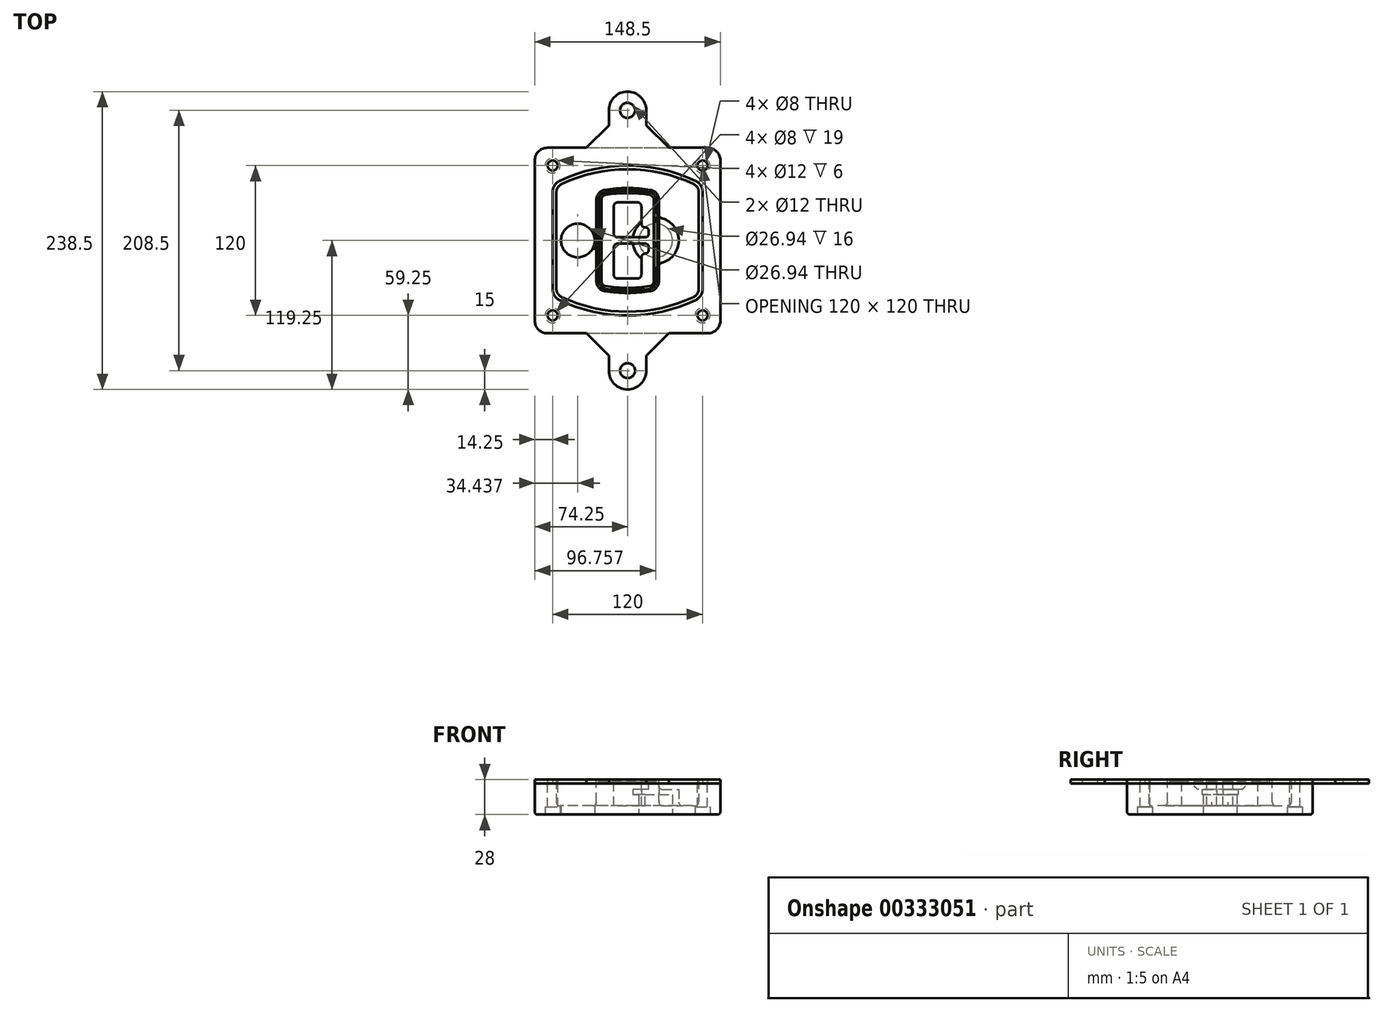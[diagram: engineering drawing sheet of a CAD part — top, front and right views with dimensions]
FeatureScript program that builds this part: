
annotation { "Feature Type Name" : "Feature", "Feature Type Description" : "" }
export const myFeature = defineFeature(function(context is Context, id is Id, definition is map)
    precondition{}
    {
        {
            var Q0;
            Q0=qCreatedBy(makeId("Top.planeOp"),FACE);
            var sketch = newSketch(context, id + "F0", { "sketchPlane" : qUnion([Q0])});
            skPoint(sketch, "E0.rect.middle", {"position": v(0, 0) * mm});
            skLineSegment(sketch, "E1.bottom", {"start": v(-64.25, -74.25) * mm, "end": v(64.25, -74.25) * mm});
            skLineSegment(sketch, "E1.top", {"start": v(-64.25, 74.25) * mm, "end": v(64.25, 74.25) * mm});
            skLineSegment(sketch, "E1.left", {"start": v(-74.25, -64.25) * mm, "end": v(-74.25, 64.25) * mm});
            skLineSegment(sketch, "E1.right", {"start": v(74.25, -64.25) * mm, "end": v(74.25, 64.25) * mm});
            skLineSegment(sketch, "E2", {"start": v(-74.25, 74.25) * mm, "end": v(74.25, -74.25) * mm, "construction": true});
            skLineSegment(sketch, "E3", {"start": v(74.25, 74.25) * mm, "end": v(-74.25, -74.25) * mm, "construction": true});
            skCircle(sketch, "E4", {"center": v(-60, 60) * mm, "radius": 4 * mm});
            skCircle(sketch, "E5", {"center": v(60, 60) * mm, "radius": 4 * mm});
            skCircle(sketch, "E6", {"center": v(60, -60) * mm, "radius": 4 * mm});
            skCircle(sketch, "E7", {"center": v(-60, -60) * mm, "radius": 4 * mm});
            skLineSegment(sketch, "E8", {"start": v(-60, 60) * mm, "end": v(60, 60) * mm, "construction": true});
            skLineSegment(sketch, "E9", {"start": v(60, 60) * mm, "end": v(60, -60) * mm, "construction": true});
            skLineSegment(sketch, "E10", {"start": v(60, -60) * mm, "end": v(-60, -60) * mm, "construction": true});
            skLineSegment(sketch, "E11", {"start": v(-60, -60) * mm, "end": v(-60, 60) * mm, "construction": true});
            skLineSegment(sketch, "E12", {"start": v(-60, 38.83) * mm, "end": v(-60, -38.83) * mm});
            skLineSegment(sketch, "E13", {"start": v(60, 38.83) * mm, "end": v(60, -38.83) * mm});
            skArc(sketch, "E14", {"start": v(54.26, 47.88) * mm, "mid": v(0, 60) * mm, "end": v(-54.26, 47.88) * mm});
            skArc(sketch, "E15", {"start": v(-54.26, -47.88) * mm, "mid": v(0, -60) * mm, "end": v(54.26, -47.88) * mm});
            skLineSegment(sketch, "E16", {"start": v(-60, 0) * mm, "end": v(60, 0) * mm, "construction": true});
            skPoint(sketch, "E17.visualSharp", {"position": v(-60, -45) * mm});
            skArc(sketch, "E17.filletArc", {"start": v(-60, -38.83) * mm, "mid": v(-58.44, -44.2) * mm, "end": v(-54.26, -47.88) * mm});
            skPoint(sketch, "E18.visualSharp", {"position": v(-60, 45) * mm});
            skArc(sketch, "E18.filletArc", {"start": v(-54.26, 47.88) * mm, "mid": v(-58.44, 44.2) * mm, "end": v(-60, 38.83) * mm});
            skPoint(sketch, "E19.visualSharp", {"position": v(60, 45) * mm});
            skArc(sketch, "E19.filletArc", {"start": v(60, 38.83) * mm, "mid": v(58.44, 44.2) * mm, "end": v(54.26, 47.88) * mm});
            skPoint(sketch, "E20.visualSharp", {"position": v(60, -45) * mm});
            skArc(sketch, "E20.filletArc", {"start": v(54.26, -47.88) * mm, "mid": v(58.44, -44.2) * mm, "end": v(60, -38.83) * mm});
            skPoint(sketch, "E21.visualSharp", {"position": v(-74.25, 74.25) * mm});
            skArc(sketch, "E21.filletArc", {"start": v(-64.25, 74.25) * mm, "mid": v(-71.32, 71.32) * mm, "end": v(-74.25, 64.25) * mm});
            skPoint(sketch, "E22.visualSharp", {"position": v(74.25, 74.25) * mm});
            skArc(sketch, "E22.filletArc", {"start": v(74.25, 64.25) * mm, "mid": v(71.32, 71.32) * mm, "end": v(64.25, 74.25) * mm});
            skPoint(sketch, "E23.visualSharp", {"position": v(74.25, -74.25) * mm});
            skArc(sketch, "E23.filletArc", {"start": v(64.25, -74.25) * mm, "mid": v(71.32, -71.32) * mm, "end": v(74.25, -64.25) * mm});
            skPoint(sketch, "E24.visualSharp", {"position": v(-74.25, -74.25) * mm});
            skArc(sketch, "E24.filletArc", {"start": v(-74.25, -64.25) * mm, "mid": v(-71.32, -71.32) * mm, "end": v(-64.25, -74.25) * mm});
            skArc(sketch, "E25.0", {"start": v(57, 38.83) * mm, "mid": v(55.9, 42.58) * mm, "end": v(52.98, 45.17) * mm});
            skLineSegment(sketch, "E25.1", {"start": v(57, 38.83) * mm, "end": v(57, -38.83) * mm});
            skArc(sketch, "E25.2", {"start": v(52.98, -45.17) * mm, "mid": v(55.9, -42.58) * mm, "end": v(57, -38.83) * mm});
            skArc(sketch, "E25.3", {"start": v(-52.98, -45.17) * mm, "mid": v(0, -57) * mm, "end": v(52.98, -45.17) * mm});
            skArc(sketch, "E25.4", {"start": v(-57, -38.83) * mm, "mid": v(-55.9, -42.58) * mm, "end": v(-52.98, -45.17) * mm});
            skArc(sketch, "E25.5", {"start": v(52.98, 45.17) * mm, "mid": v(0, 57) * mm, "end": v(-52.98, 45.17) * mm});
            skLineSegment(sketch, "E25.6", {"start": v(-57, 38.83) * mm, "end": v(-57, -38.83) * mm});
            skArc(sketch, "E25.7", {"start": v(-52.98, 45.17) * mm, "mid": v(-55.9, 42.58) * mm, "end": v(-57, 38.83) * mm});
            skArc(sketch, "E26.0", {"start": v(-55.96, 51.5) * mm, "mid": v(-61.82, 46.33) * mm, "end": v(-64, 38.83) * mm});
            skArc(sketch, "E26.1", {"start": v(55.96, 51.5) * mm, "mid": v(0, 64) * mm, "end": v(-55.96, 51.5) * mm});
            skArc(sketch, "E26.2", {"start": v(64, 38.83) * mm, "mid": v(61.82, 46.33) * mm, "end": v(55.96, 51.5) * mm});
            skLineSegment(sketch, "E26.3", {"start": v(64, 38.83) * mm, "end": v(64, -38.83) * mm});
            skArc(sketch, "E26.4", {"start": v(55.96, -51.5) * mm, "mid": v(61.82, -46.33) * mm, "end": v(64, -38.83) * mm});
            skLineSegment(sketch, "E26.5", {"start": v(-64, 38.83) * mm, "end": v(-64, -38.83) * mm});
            skArc(sketch, "E26.6", {"start": v(-55.96, -51.5) * mm, "mid": v(0, -64) * mm, "end": v(55.96, -51.5) * mm});
            skArc(sketch, "E26.7", {"start": v(-64, -38.83) * mm, "mid": v(-61.82, -46.33) * mm, "end": v(-55.96, -51.5) * mm});
            skSolve(sketch);
        }
        {
            var Q0;
            Q0=makeQuery(id+"F0.imprint","IMPRINT",FACE,{"disambiguationData":[TD([[makeQuery(id+"F0.imprint","IMPRINT",EDGE,{"derivedFrom":sQuery(id+"F0.wireOp",EDGE,"E1.bottom")}),1.0]])]});
            var Q1;
            Q1=makeQuery(id+"F0.imprint","IMPRINT",FACE,{"disambiguationData":[TD([[makeQuery(id+"F0.imprint","IMPRINT",EDGE,{"derivedFrom":sQuery(id+"F0.wireOp",EDGE,"E12")}),1.0]])]});
            var Q2;
            Q2=makeQuery(id+"F0.imprint","IMPRINT",FACE,{"disambiguationData":[TD([[makeQuery(id+"F0.imprint","IMPRINT",EDGE,{"derivedFrom":sQuery(id+"F0.wireOp",EDGE,"E25.0")}),1.0]])]});
            var Q3;
            Q3=makeQuery(id+"F0.imprint","IMPRINT",FACE,{"disambiguationData":[TD([[makeQuery(id+"F0.imprint","IMPRINT",EDGE,{"derivedFrom":sQuery(id+"F0.wireOp",EDGE,"E12")}),-1.0]])]});
            extrude(context, id + "F1", {"entities" : qUnion([Q0, Q1, Q2, Q3]), "oppositeDirection" : true, "depth" : 25 * mm});
        }
        {
            var Q0;
            Q0=makeQuery(id+"F0.imprint","IMPRINT",FACE,{"disambiguationData":[TD([[makeQuery(id+"F0.imprint","IMPRINT",EDGE,{"derivedFrom":sQuery(id+"F0.wireOp",EDGE,"E12")}),1.0]])]});
            extrude(context, id + "F2", {"entities" : qUnion([Q0]), "operationType" : NewBodyOperationType.ADD, "depth" : 3 * mm});
        }
        {
            var Q0;
            Q0=makeQuery(id+"F0.imprint","IMPRINT",FACE,{"disambiguationData":[TD([[makeQuery(id+"F0.imprint","IMPRINT",EDGE,{"derivedFrom":sQuery(id+"F0.wireOp",EDGE,"E25.0")}),1.0]])]});
            extrude(context, id + "F3", {"entities" : qUnion([Q0]), "operationType" : NewBodyOperationType.REMOVE, "oppositeDirection" : true, "depth" : 18 * mm});
        }
        {
            var Q0;
            Q0=makeQuery(id+"F2.opExtrude","CAP_FACE",FACE,{"disambiguationData":[OSD([sQuery(id+"F0.wireOp",EDGE,"E12"),sQuery(id+"F0.wireOp",EDGE,"E13"),sQuery(id+"F0.wireOp",EDGE,"E14"),sQuery(id+"F0.wireOp",EDGE,"E15"),sQuery(id+"F0.wireOp",EDGE,"E17.filletArc"),sQuery(id+"F0.wireOp",EDGE,"E18.filletArc"),sQuery(id+"F0.wireOp",EDGE,"E19.filletArc"),sQuery(id+"F0.wireOp",EDGE,"E20.filletArc"),sQuery(id+"F0.wireOp",EDGE,"E25.0"),sQuery(id+"F0.wireOp",EDGE,"E25.1"),sQuery(id+"F0.wireOp",EDGE,"E25.2"),sQuery(id+"F0.wireOp",EDGE,"E25.3"),sQuery(id+"F0.wireOp",EDGE,"E25.4"),sQuery(id+"F0.wireOp",EDGE,"E25.5"),sQuery(id+"F0.wireOp",EDGE,"E25.6"),sQuery(id+"F0.wireOp",EDGE,"E25.7")])],"isStart":false});
            var sketch = newSketch(context, id + "F4", { "sketchPlane" : qUnion([Q0])});
            skArc(sketch, "E27.0", {"start": v(-18.34, -40.45) * mm, "mid": v(0, -42) * mm, "end": v(18.34, -40.45) * mm});
            skArc(sketch, "E28.0", {"start": v(18.34, 40.45) * mm, "mid": v(0, 42) * mm, "end": v(-18.34, 40.45) * mm});
            skLineSegment(sketch, "E29", {"start": v(-25, 32.57) * mm, "end": v(-25, -32.57) * mm});
            skLineSegment(sketch, "E30", {"start": v(25, 32.57) * mm, "end": v(25, -32.57) * mm});
            skLineSegment(sketch, "E31", {"start": v(-25, 39.1) * mm, "end": v(25, 39.1) * mm, "construction": true});
            skLineSegment(sketch, "E32", {"start": v(-25, -39.1) * mm, "end": v(25, -39.1) * mm, "construction": true});
            skPoint(sketch, "E33.visualSharp", {"position": v(-25, 39.1) * mm});
            skArc(sketch, "E33.filletArc", {"start": v(-18.34, 40.45) * mm, "mid": v(-23.11, 37.73) * mm, "end": v(-25, 32.57) * mm});
            skPoint(sketch, "E34.visualSharp", {"position": v(25, 39.1) * mm});
            skArc(sketch, "E34.filletArc", {"start": v(25, 32.57) * mm, "mid": v(23.11, 37.73) * mm, "end": v(18.34, 40.45) * mm});
            skPoint(sketch, "E35.visualSharp", {"position": v(25, -39.1) * mm});
            skArc(sketch, "E35.filletArc", {"start": v(18.34, -40.45) * mm, "mid": v(23.11, -37.73) * mm, "end": v(25, -32.57) * mm});
            skPoint(sketch, "E36.visualSharp", {"position": v(-25, -39.1) * mm});
            skArc(sketch, "E36.filletArc", {"start": v(-25, -32.57) * mm, "mid": v(-23.11, -37.73) * mm, "end": v(-18.34, -40.45) * mm});
            skArc(sketch, "E37.0", {"start": v(52.98, 45.17) * mm, "mid": v(0, 57) * mm, "end": v(-52.98, 45.17) * mm});
            skArc(sketch, "E37.1", {"start": v(-52.98, 45.17) * mm, "mid": v(-55.9, 42.58) * mm, "end": v(-57, 38.83) * mm});
            skLineSegment(sketch, "E37.2", {"start": v(-57, 38.83) * mm, "end": v(-57, -38.83) * mm});
            skArc(sketch, "E37.3", {"start": v(-57, -38.83) * mm, "mid": v(-55.9, -42.58) * mm, "end": v(-52.98, -45.17) * mm});
            skArc(sketch, "E37.4", {"start": v(-52.98, -45.17) * mm, "mid": v(0, -57) * mm, "end": v(52.98, -45.17) * mm});
            skArc(sketch, "E37.5", {"start": v(52.98, -45.17) * mm, "mid": v(55.9, -42.58) * mm, "end": v(57, -38.83) * mm});
            skLineSegment(sketch, "E37.6", {"start": v(57, 38.83) * mm, "end": v(57, -38.83) * mm});
            skArc(sketch, "E37.7", {"start": v(57, 38.83) * mm, "mid": v(55.9, 42.58) * mm, "end": v(52.98, 45.17) * mm});
            skLineSegment(sketch, "E38.0", {"start": v(23, 32.57) * mm, "end": v(23, -32.57) * mm});
            skArc(sketch, "E38.1", {"start": v(18, -38.48) * mm, "mid": v(21.58, -36.44) * mm, "end": v(23, -32.57) * mm});
            skArc(sketch, "E38.2", {"start": v(-18, -38.48) * mm, "mid": v(0, -40) * mm, "end": v(18, -38.48) * mm});
            skArc(sketch, "E38.3", {"start": v(-23, -32.57) * mm, "mid": v(-21.58, -36.44) * mm, "end": v(-18, -38.48) * mm});
            skLineSegment(sketch, "E38.4", {"start": v(-23, 32.57) * mm, "end": v(-23, -32.57) * mm});
            skArc(sketch, "E38.5", {"start": v(23, 32.57) * mm, "mid": v(21.58, 36.44) * mm, "end": v(18, 38.48) * mm});
            skArc(sketch, "E38.6", {"start": v(-18, 38.48) * mm, "mid": v(-21.58, 36.44) * mm, "end": v(-23, 32.57) * mm});
            skArc(sketch, "E38.7", {"start": v(18, 38.48) * mm, "mid": v(0, 40) * mm, "end": v(-18, 38.48) * mm});
            skArc(sketch, "E39.0", {"start": v(21, 32.57) * mm, "mid": v(20.06, 35.15) * mm, "end": v(17.67, 36.5) * mm});
            skLineSegment(sketch, "E39.1", {"start": v(21, 32.57) * mm, "end": v(21, -32.57) * mm});
            skArc(sketch, "E39.2", {"start": v(17.67, -36.5) * mm, "mid": v(20.06, -35.15) * mm, "end": v(21, -32.57) * mm});
            skArc(sketch, "E39.3", {"start": v(-17.67, -36.5) * mm, "mid": v(0, -38) * mm, "end": v(17.67, -36.5) * mm});
            skArc(sketch, "E39.4", {"start": v(-21, -32.57) * mm, "mid": v(-20.06, -35.15) * mm, "end": v(-17.67, -36.5) * mm});
            skArc(sketch, "E39.5", {"start": v(17.67, 36.5) * mm, "mid": v(0, 38) * mm, "end": v(-17.67, 36.5) * mm});
            skLineSegment(sketch, "E39.6", {"start": v(-21, 32.57) * mm, "end": v(-21, -32.57) * mm});
            skArc(sketch, "E39.7", {"start": v(-17.67, 36.5) * mm, "mid": v(-20.06, 35.15) * mm, "end": v(-21, 32.57) * mm});
            skLineSegment(sketch, "E40", {"start": v(-25, 0) * mm, "end": v(25, 0) * mm, "construction": true});
            skLineSegment(sketch, "E41", {"start": v(-11, 5.5) * mm, "end": v(-11, 27.5) * mm});
            skLineSegment(sketch, "E42", {"start": v(-8, 30.5) * mm, "end": v(8, 30.5) * mm});
            skLineSegment(sketch, "E43", {"start": v(11, 27.5) * mm, "end": v(11, 13.5) * mm});
            skLineSegment(sketch, "E44", {"start": v(14, 10.5) * mm, "end": v(14, 10.5) * mm});
            skLineSegment(sketch, "E45", {"start": v(17, 7.5) * mm, "end": v(17, 5.5) * mm});
            skLineSegment(sketch, "E46", {"start": v(14, 2.5) * mm, "end": v(-8, 2.5) * mm});
            skPoint(sketch, "E47.visualSharp", {"position": v(-11, 30.5) * mm});
            skArc(sketch, "E47.filletArc", {"start": v(-8, 30.5) * mm, "mid": v(-10.12, 29.62) * mm, "end": v(-11, 27.5) * mm});
            skPoint(sketch, "E48.visualSharp", {"position": v(11, 30.5) * mm});
            skArc(sketch, "E48.filletArc", {"start": v(11, 27.5) * mm, "mid": v(10.12, 29.62) * mm, "end": v(8, 30.5) * mm});
            skPoint(sketch, "E49.visualSharp", {"position": v(11, 10.5) * mm});
            skArc(sketch, "E49.filletArc", {"start": v(11, 13.5) * mm, "mid": v(11.88, 11.38) * mm, "end": v(14, 10.5) * mm});
            skPoint(sketch, "E50.visualSharp", {"position": v(17, 10.5) * mm});
            skArc(sketch, "E50.filletArc", {"start": v(17, 7.5) * mm, "mid": v(16.12, 9.62) * mm, "end": v(14, 10.5) * mm});
            skPoint(sketch, "E51.visualSharp", {"position": v(17, 2.5) * mm});
            skArc(sketch, "E51.filletArc", {"start": v(14, 2.5) * mm, "mid": v(16.12, 3.38) * mm, "end": v(17, 5.5) * mm});
            skPoint(sketch, "E52.visualSharp", {"position": v(-11, 2.5) * mm});
            skArc(sketch, "E52.filletArc", {"start": v(-11, 5.5) * mm, "mid": v(-10.12, 3.38) * mm, "end": v(-8, 2.5) * mm});
            skLineSegment(sketch, "E53.0.MirrorCS", {"start": v(14, -2.5) * mm, "end": v(-8, -2.5) * mm});
            skArc(sketch, "E54.0.MirrorCS", {"start": v(-11, -5.5) * mm, "mid": v(-10.12, -3.38) * mm, "end": v(-8, -2.5) * mm});
            skLineSegment(sketch, "E55.0.MirrorCS", {"start": v(-11, -5.5) * mm, "end": v(-11, -27.5) * mm});
            skArc(sketch, "E56.0.MirrorCS", {"start": v(-8, -30.5) * mm, "mid": v(-10.12, -29.62) * mm, "end": v(-11, -27.5) * mm});
            skLineSegment(sketch, "E57.0.MirrorCS", {"start": v(-8, -30.5) * mm, "end": v(8, -30.5) * mm});
            skArc(sketch, "E58.0.MirrorCS", {"start": v(11, -27.5) * mm, "mid": v(10.12, -29.62) * mm, "end": v(8, -30.5) * mm});
            skLineSegment(sketch, "E59.0.MirrorCS", {"start": v(11, -27.5) * mm, "end": v(11, -13.5) * mm});
            skArc(sketch, "E60.0.MirrorCS", {"start": v(11, -13.5) * mm, "mid": v(11.88, -11.38) * mm, "end": v(14, -10.5) * mm});
            skArc(sketch, "E61.0.MirrorCS", {"start": v(17, -7.5) * mm, "mid": v(16.12, -9.62) * mm, "end": v(14, -10.5) * mm});
            skLineSegment(sketch, "E62.0.MirrorCS", {"start": v(17, -7.5) * mm, "end": v(17, -5.5) * mm});
            skArc(sketch, "E63.0.MirrorCS", {"start": v(14, -2.5) * mm, "mid": v(16.12, -3.38) * mm, "end": v(17, -5.5) * mm});
            skSolve(sketch);
        }
        {
            var Q0;
            Q0=makeQuery(id+"F4.imprint","IMPRINT",FACE,{"disambiguationData":[TD([[makeQuery(id+"F4.imprint","IMPRINT",EDGE,{"derivedFrom":sQuery(id+"F4.wireOp",EDGE,"E27.0")}),1.0]])]});
            var Q1;
            Q1=makeQuery(id+"F4.imprint","IMPRINT",FACE,{"disambiguationData":[TD([[makeQuery(id+"F4.imprint","IMPRINT",EDGE,{"derivedFrom":sQuery(id+"F4.wireOp",EDGE,"E38.0")}),-1.0]])]});
            var Q2;
            Q2=makeQuery(id+"F4.imprint","IMPRINT",FACE,{"disambiguationData":[TD([[makeQuery(id+"F4.imprint","IMPRINT",EDGE,{"derivedFrom":sQuery(id+"F4.wireOp",EDGE,"E39.0")}),1.0]])]});
            extrude(context, id + "F5", {"entities" : qUnion([Q0, Q1, Q2]), "operationType" : NewBodyOperationType.ADD, "endBound" : BoundingType.UP_TO_NEXT, "oppositeDirection" : true, "depth" : 25 * mm});
        }
        {
            var Q0;
            Q0=makeQuery(id+"F4.imprint","IMPRINT",FACE,{"disambiguationData":[TD([[makeQuery(id+"F4.imprint","IMPRINT",EDGE,{"derivedFrom":sQuery(id+"F4.wireOp",EDGE,"E38.0")}),-1.0]])]});
            extrude(context, id + "F6", {"entities" : qUnion([Q0]), "operationType" : NewBodyOperationType.REMOVE, "oppositeDirection" : true, "depth" : 2 * mm});
        }
        {
            var Q0;
            Q0=makeQuery(id+"F1.opExtrude","CAP_FACE",FACE,{"disambiguationData":[OSD([sQuery(id+"F0.wireOp",EDGE,"E1.bottom"),sQuery(id+"F0.wireOp",EDGE,"E1.top"),sQuery(id+"F0.wireOp",EDGE,"E1.left"),sQuery(id+"F0.wireOp",EDGE,"E1.right"),sQuery(id+"F0.wireOp",EDGE,"E4"),sQuery(id+"F0.wireOp",EDGE,"E5"),sQuery(id+"F0.wireOp",EDGE,"E6"),sQuery(id+"F0.wireOp",EDGE,"E7"),sQuery(id+"F0.wireOp",EDGE,"E21.filletArc"),sQuery(id+"F0.wireOp",EDGE,"E22.filletArc"),sQuery(id+"F0.wireOp",EDGE,"E23.filletArc"),sQuery(id+"F0.wireOp",EDGE,"E24.filletArc")])],"isStart":false});
            var sketch = newSketch(context, id + "F7", { "sketchPlane" : qUnion([Q0])});
            skCircle(sketch, "E64", {"center": v(22.5, 0) * mm, "radius": 13.47 * mm});
            skCircle(sketch, "E65", {"center": v(-39.81, 0) * mm, "radius": 13.47 * mm});
            skLineSegment(sketch, "E66", {"start": v(74.25, 0) * mm, "end": v(-74.25, 0) * mm});
            skCircle(sketch, "E67", {"center": v(22.5, 0) * mm, "radius": 18.47 * mm});
            skCircle(sketch, "E68", {"center": v(60, -60) * mm, "radius": 6 * mm});
            skCircle(sketch, "E69", {"center": v(-60, -60) * mm, "radius": 6 * mm});
            skCircle(sketch, "E70", {"center": v(-60, 60) * mm, "radius": 6 * mm});
            skCircle(sketch, "E71", {"center": v(60, 60) * mm, "radius": 6 * mm});
            skSolve(sketch);
        }
        {
            var Q0;
            {var subQ1=sQuery(id+"F7.wireOp",EDGE,"E66");var subQ4=sQuery(id+"F7.wireOp",EDGE,"E64");var subQ6=makeQuery(id+"F7.imprint","INTERSECT",VERTEX,{"disambiguationData":[OD(0.0)],"derivedFrom":[subQ4,subQ1]});Q0=makeQuery(id+"F7.imprint","IMPRINT",FACE,{"disambiguationData":[TD([[makeQuery(id+"F7.imprint","IMPRINT",EDGE,{"disambiguationData":[TD([[subQ6,-1.0]])],"derivedFrom":subQ4}),-1.0]])]});}
            var Q1;
            {var subQ0=sQuery(id+"F7.wireOp",EDGE,"E66");var subQ1=sQuery(id+"F7.wireOp",EDGE,"E64");var subQ3=makeQuery(id+"F7.imprint","INTERSECT",VERTEX,{"disambiguationData":[OD(0.0)],"derivedFrom":[subQ1,subQ0]});Q1=makeQuery(id+"F7.imprint","IMPRINT",FACE,{"disambiguationData":[TD([[makeQuery(id+"F7.imprint","IMPRINT",EDGE,{"disambiguationData":[TD([[subQ3,-1.0]])],"derivedFrom":subQ1}),1.0]])]});}
            var Q2;
            {var subQ0=sQuery(id+"F7.wireOp",EDGE,"E66");var subQ1=sQuery(id+"F7.wireOp",EDGE,"E64");var subQ3=makeQuery(id+"F7.imprint","INTERSECT",VERTEX,{"disambiguationData":[OD(0.0)],"derivedFrom":[subQ1,subQ0]});Q2=makeQuery(id+"F7.imprint","IMPRINT",FACE,{"disambiguationData":[TD([[makeQuery(id+"F7.imprint","IMPRINT",EDGE,{"disambiguationData":[TD([[subQ3,1.0]])],"derivedFrom":subQ1}),1.0]])]});}
            var Q3;
            {var subQ1=sQuery(id+"F7.wireOp",EDGE,"E66");var subQ4=sQuery(id+"F7.wireOp",EDGE,"E64");var subQ6=makeQuery(id+"F7.imprint","INTERSECT",VERTEX,{"disambiguationData":[OD(0.0)],"derivedFrom":[subQ4,subQ1]});Q3=makeQuery(id+"F7.imprint","IMPRINT",FACE,{"disambiguationData":[TD([[makeQuery(id+"F7.imprint","IMPRINT",EDGE,{"disambiguationData":[TD([[subQ6,1.0]])],"derivedFrom":subQ4}),-1.0]])]});}
            extrude(context, id + "F8", {"entities" : qUnion([Q0, Q1, Q2, Q3]), "operationType" : NewBodyOperationType.ADD, "oppositeDirection" : true, "depth" : 20 * mm});
        }
        {
            var Q0;
            {var subQ0=sQuery(id+"F7.wireOp",EDGE,"E66");var subQ1=sQuery(id+"F7.wireOp",EDGE,"E64");var subQ3=makeQuery(id+"F7.imprint","INTERSECT",VERTEX,{"disambiguationData":[OD(0.0)],"derivedFrom":[subQ1,subQ0]});Q0=makeQuery(id+"F7.imprint","IMPRINT",FACE,{"disambiguationData":[TD([[makeQuery(id+"F7.imprint","IMPRINT",EDGE,{"disambiguationData":[TD([[subQ3,-1.0]])],"derivedFrom":subQ1}),1.0]])]});}
            var Q1;
            {var subQ0=sQuery(id+"F7.wireOp",EDGE,"E66");var subQ1=sQuery(id+"F7.wireOp",EDGE,"E64");var subQ3=makeQuery(id+"F7.imprint","INTERSECT",VERTEX,{"disambiguationData":[OD(0.0)],"derivedFrom":[subQ1,subQ0]});Q1=makeQuery(id+"F7.imprint","IMPRINT",FACE,{"disambiguationData":[TD([[makeQuery(id+"F7.imprint","IMPRINT",EDGE,{"disambiguationData":[TD([[subQ3,1.0]])],"derivedFrom":subQ1}),1.0]])]});}
            extrude(context, id + "F9", {"entities" : qUnion([Q0, Q1]), "operationType" : NewBodyOperationType.REMOVE, "oppositeDirection" : true, "depth" : 16 * mm});
        }
        {
            var Q0;
            {var subQ0=sQuery(id+"F7.wireOp",EDGE,"E66");var subQ1=sQuery(id+"F7.wireOp",EDGE,"E65");var subQ3=makeQuery(id+"F7.imprint","INTERSECT",VERTEX,{"disambiguationData":[OD(0.0)],"derivedFrom":[subQ1,subQ0]});Q0=makeQuery(id+"F7.imprint","IMPRINT",FACE,{"disambiguationData":[TD([[makeQuery(id+"F7.imprint","IMPRINT",EDGE,{"disambiguationData":[TD([[subQ3,-1.0]])],"derivedFrom":subQ1}),1.0]])]});}
            var Q1;
            {var subQ0=sQuery(id+"F7.wireOp",EDGE,"E66");var subQ1=sQuery(id+"F7.wireOp",EDGE,"E65");var subQ3=makeQuery(id+"F7.imprint","INTERSECT",VERTEX,{"disambiguationData":[OD(0.0)],"derivedFrom":[subQ1,subQ0]});Q1=makeQuery(id+"F7.imprint","IMPRINT",FACE,{"disambiguationData":[TD([[makeQuery(id+"F7.imprint","IMPRINT",EDGE,{"disambiguationData":[TD([[subQ3,1.0]])],"derivedFrom":subQ1}),1.0]])]});}
            extrude(context, id + "F10", {"entities" : qUnion([Q0, Q1]), "operationType" : NewBodyOperationType.REMOVE, "oppositeDirection" : true, "depth" : 25 * mm});
        }
        {
            var Q0;
            Q0=makeQuery(id+"F7.imprint","IMPRINT",FACE,{"disambiguationData":[TD([[makeQuery(id+"F7.imprint","IMPRINT",EDGE,{"derivedFrom":sQuery(id+"F7.wireOp",EDGE,"E68")}),1.0]])]});
            var Q1;
            Q1=makeQuery(id+"F7.imprint","IMPRINT",FACE,{"disambiguationData":[TD([[makeQuery(id+"F7.imprint","IMPRINT",EDGE,{"derivedFrom":makeQuery(id+"F1.opExtrude","CAP_EDGE",EDGE,{"disambiguationData":[OSD([sQuery(id+"F0.wireOp",EDGE,"E5")])],"isStart":false})}),-1.0]])]});
            var Q2;
            Q2=makeQuery(id+"F7.imprint","IMPRINT",FACE,{"disambiguationData":[TD([[makeQuery(id+"F7.imprint","IMPRINT",EDGE,{"derivedFrom":sQuery(id+"F7.wireOp",EDGE,"E69")}),1.0]])]});
            var Q3;
            Q3=makeQuery(id+"F7.imprint","IMPRINT",FACE,{"disambiguationData":[TD([[makeQuery(id+"F7.imprint","IMPRINT",EDGE,{"derivedFrom":makeQuery(id+"F1.opExtrude","CAP_EDGE",EDGE,{"disambiguationData":[OSD([sQuery(id+"F0.wireOp",EDGE,"E4")])],"isStart":false})}),-1.0]])]});
            var Q4;
            Q4=makeQuery(id+"F7.imprint","IMPRINT",FACE,{"disambiguationData":[TD([[makeQuery(id+"F7.imprint","IMPRINT",EDGE,{"derivedFrom":sQuery(id+"F7.wireOp",EDGE,"E70")}),1.0]])]});
            var Q5;
            Q5=makeQuery(id+"F7.imprint","IMPRINT",FACE,{"disambiguationData":[TD([[makeQuery(id+"F7.imprint","IMPRINT",EDGE,{"derivedFrom":makeQuery(id+"F1.opExtrude","CAP_EDGE",EDGE,{"disambiguationData":[OSD([sQuery(id+"F0.wireOp",EDGE,"E7")])],"isStart":false})}),-1.0]])]});
            var Q6;
            Q6=makeQuery(id+"F7.imprint","IMPRINT",FACE,{"disambiguationData":[TD([[makeQuery(id+"F7.imprint","IMPRINT",EDGE,{"derivedFrom":sQuery(id+"F7.wireOp",EDGE,"E71")}),1.0]])]});
            var Q7;
            Q7=makeQuery(id+"F7.imprint","IMPRINT",FACE,{"disambiguationData":[TD([[makeQuery(id+"F7.imprint","IMPRINT",EDGE,{"derivedFrom":makeQuery(id+"F1.opExtrude","CAP_EDGE",EDGE,{"disambiguationData":[OSD([sQuery(id+"F0.wireOp",EDGE,"E6")])],"isStart":false})}),-1.0]])]});
            extrude(context, id + "F11", {"entities" : qUnion([Q0, Q1, Q2, Q3, Q4, Q5, Q6, Q7]), "operationType" : NewBodyOperationType.REMOVE, "oppositeDirection" : true, "depth" : 6 * mm});
        }
        {
            var Q0;
            Q0=makeQuery(id+"F9.boolean.opBoolean","COPY",FACE,{"derivedFrom":makeQuery(id+"F9.opExtrude","CAP_FACE",FACE,{"disambiguationData":[OSD([sQuery(id+"F7.wireOp",EDGE,"E64")])],"isStart":false})});
            var sketch = newSketch(context, id + "F12", { "sketchPlane" : qUnion([Q0])});
            skArc(sketch, "E72.0", {"start": v(11, 14.45) * mm, "mid": v(6.45, 9.13) * mm, "end": v(4.2, 2.5) * mm});
            skArc(sketch, "E72.1", {"start": v(4.2, -2.5) * mm, "mid": v(6.45, -9.13) * mm, "end": v(11, -14.45) * mm});
            skLineSegment(sketch, "E73", {"start": v(4.2, -2.5) * mm, "end": v(14, -2.5) * mm});
            skLineSegment(sketch, "E74.0", {"start": v(14, 2.5) * mm, "end": v(4.2, 2.5) * mm});
            skArc(sketch, "E74.1", {"start": v(14, 2.5) * mm, "mid": v(16.12, 3.38) * mm, "end": v(17, 5.5) * mm});
            skLineSegment(sketch, "E74.2", {"start": v(17, 7.5) * mm, "end": v(17, 5.5) * mm});
            skArc(sketch, "E74.3", {"start": v(17, 7.5) * mm, "mid": v(16.12, 9.62) * mm, "end": v(14, 10.5) * mm});
            skArc(sketch, "E74.4", {"start": v(11, 13.5) * mm, "mid": v(11.88, 11.38) * mm, "end": v(14, 10.5) * mm});
            skLineSegment(sketch, "E74.5", {"start": v(11, 14.45) * mm, "end": v(11, 13.5) * mm});
            skLineSegment(sketch, "E74.7", {"start": v(14, -2.5) * mm, "end": v(4.2, -2.5) * mm});
            skArc(sketch, "E74.8", {"start": v(14, -2.5) * mm, "mid": v(16.12, -3.38) * mm, "end": v(17, -5.5) * mm});
            skLineSegment(sketch, "E74.9", {"start": v(17, -7.5) * mm, "end": v(17, -5.5) * mm});
            skArc(sketch, "E74.10", {"start": v(17, -7.5) * mm, "mid": v(16.12, -9.62) * mm, "end": v(14, -10.5) * mm});
            skArc(sketch, "E74.11", {"start": v(11, -13.5) * mm, "mid": v(11.88, -11.38) * mm, "end": v(14, -10.5) * mm});
            skLineSegment(sketch, "E74.12", {"start": v(11, -14.45) * mm, "end": v(11, -13.5) * mm});
            skPoint(sketch, "E75.orphan", {"position": v(11, -27.5) * mm});
            skPoint(sketch, "E76.orphan", {"position": v(-8, -2.5) * mm});
            skPoint(sketch, "E77.orphan", {"position": v(-8, 2.5) * mm});
            skPoint(sketch, "E78.orphan", {"position": v(11, 27.5) * mm});
            skSolve(sketch);
        }
        {
            var Q0;
            {var subQ7=sQuery(id+"F12.wireOp",EDGE,"E72.0");var subQ14=sQuery(id+"F12.wireOp",EDGE,"E72.1");var subQ16=sQuery(id+"F12.wireOp",EDGE,"E74.1");var subQ18=sQuery(id+"F12.wireOp",EDGE,"E74.8");Q0=qUnion([makeQuery(id+"F12.imprint","IMPRINT",FACE,{"disambiguationData":[TD([[makeQuery(id+"F12.imprint","IMPRINT",EDGE,{"derivedFrom":subQ7}),1.0]])]}),makeQuery(id+"F12.imprint","IMPRINT",FACE,{"disambiguationData":[TD([[makeQuery(id+"F12.imprint","IMPRINT",EDGE,{"derivedFrom":subQ14}),1.0]])]}),makeQuery(id+"F12.imprint","IMPRINT",FACE,{"disambiguationData":[TD([[makeQuery(id+"F12.imprint","IMPRINT",EDGE,{"derivedFrom":subQ16}),1.0]])]}),makeQuery(id+"F12.imprint","IMPRINT",FACE,{"disambiguationData":[TD([[makeQuery(id+"F12.imprint","IMPRINT",EDGE,{"derivedFrom":subQ18}),-1.0]])]})]);}
            var Q1;
            Q1=makeQuery(id+"F5.boolean.opBoolean","SPLIT",FACE,{"disambiguationData":[TD([makeQuery(id+"F5.opExtrude","SWEPT_FACE",FACE,{"disambiguationData":[OSD([sQuery(id+"F4.wireOp",EDGE,"E41")])]})])],"derivedFrom":makeQuery(id+"F3.boolean.opBoolean","COPY",FACE,{"derivedFrom":makeQuery(id+"F3.opExtrude","CAP_FACE",FACE,{"disambiguationData":[OSD([sQuery(id+"F0.wireOp",EDGE,"E25.0"),sQuery(id+"F0.wireOp",EDGE,"E25.1"),sQuery(id+"F0.wireOp",EDGE,"E25.2"),sQuery(id+"F0.wireOp",EDGE,"E25.3"),sQuery(id+"F0.wireOp",EDGE,"E25.4"),sQuery(id+"F0.wireOp",EDGE,"E25.5"),sQuery(id+"F0.wireOp",EDGE,"E25.6"),sQuery(id+"F0.wireOp",EDGE,"E25.7")])],"isStart":false})})});
            extrude(context, id + "F13", {"entities" : qUnion([Q0]), "operationType" : NewBodyOperationType.REMOVE, "endBound" : BoundingType.UP_TO_SURFACE, "endBoundEntityFace" : qUnion([Q1]), "depth" : 25 * mm});
        }
        {
            var Q0;
            Q0=makeQuery(id+"F3.boolean.opBoolean","COPY",EDGE,{"derivedFrom":makeQuery(id+"F3.opExtrude","CAP_EDGE",EDGE,{"disambiguationData":[OSD([sQuery(id+"F0.wireOp",EDGE,"E25.6")])],"isStart":false})});
            var Q1;
            Q1=makeQuery(id+"F8.boolean.opBoolean","INTERSECT",EDGE,{"derivedFrom":[makeQuery(id+"F5.opExtrude","SWEPT_FACE",FACE,{"disambiguationData":[OSD([sQuery(id+"F4.wireOp",EDGE,"E30")])]}),makeQuery(id+"F8.opExtrude","CAP_FACE",FACE,{"disambiguationData":[OSD([sQuery(id+"F7.wireOp",EDGE,"E67")])],"isStart":false})]});
            var Q2;
            Q2=makeQuery(id+"F8.boolean.opBoolean","INTERSECT",EDGE,{"disambiguationData":[OD(1.0)],"derivedFrom":[makeQuery(id+"F5.opExtrude","SWEPT_FACE",FACE,{"disambiguationData":[OSD([sQuery(id+"F4.wireOp",EDGE,"E30")])]}),makeQuery(id+"F8.opExtrude","SWEPT_FACE",FACE,{"disambiguationData":[OSD([sQuery(id+"F7.wireOp",EDGE,"E67")])]})]});
            var Q3;
            {var subQ0=sQuery(id+"F4.wireOp",EDGE,"E30");Q3=makeQuery(id+"F8.boolean.opBoolean","SPLIT",EDGE,{"disambiguationData":[TD([makeQuery(id+"F5.opExtrude","SWEPT_FACE",FACE,{"disambiguationData":[OSD([sQuery(id+"F4.wireOp",EDGE,"E35.filletArc")])]})])],"derivedFrom":makeQuery(id+"F5.opExtrude","CAP_EDGE",EDGE,{"disambiguationData":[OSD([subQ0])],"isStart":false})});}
            var Q4;
            {var subQ0=sQuery(id+"F0.wireOp",EDGE,"E25.7");var subQ1=sQuery(id+"F0.wireOp",EDGE,"E25.1");var subQ2=sQuery(id+"F0.wireOp",EDGE,"E25.6");var subQ3=sQuery(id+"F0.wireOp",EDGE,"E25.5");var subQ4=sQuery(id+"F0.wireOp",EDGE,"E25.4");var subQ5=sQuery(id+"F0.wireOp",EDGE,"E25.0");var subQ6=sQuery(id+"F0.wireOp",EDGE,"E25.2");var subQ7=sQuery(id+"F0.wireOp",EDGE,"E25.3");Q4=makeQuery(id+"F8.boolean.opBoolean","INTERSECT",EDGE,{"derivedFrom":[makeQuery(id+"F5.boolean.opBoolean","SPLIT",FACE,{"disambiguationData":[TD([makeQuery(id+"F2.opExtrude","SWEPT_FACE",FACE,{"disambiguationData":[OSD([subQ5])]})])],"derivedFrom":makeQuery(id+"F3.boolean.opBoolean","COPY",FACE,{"derivedFrom":makeQuery(id+"F3.opExtrude","CAP_FACE",FACE,{"disambiguationData":[OSD([subQ5,subQ1,subQ6,subQ7,subQ4,subQ3,subQ2,subQ0])],"isStart":false})})}),makeQuery(id+"F8.opExtrude","SWEPT_FACE",FACE,{"disambiguationData":[OSD([sQuery(id+"F7.wireOp",EDGE,"E67")])]})]});}
            var Q5;
            Q5=makeQuery(id+"F8.boolean.opBoolean","INTERSECT",EDGE,{"disambiguationData":[OD(0.0)],"derivedFrom":[makeQuery(id+"F5.opExtrude","SWEPT_FACE",FACE,{"disambiguationData":[OSD([sQuery(id+"F4.wireOp",EDGE,"E30")])]}),makeQuery(id+"F8.opExtrude","SWEPT_FACE",FACE,{"disambiguationData":[OSD([sQuery(id+"F7.wireOp",EDGE,"E67")])]})]});
            fillet(context, id + "F14", {"entities" : qUnion([Q0, Q1, Q2, Q3, Q4, Q5]), "radius" : 3 * mm, "tangentPropagation" : true, "allowEdgeOverflow" : false});
        }
        {
            var Q0;
            Q0=makeQuery(id+"F1.opExtrude","CAP_EDGE",EDGE,{"disambiguationData":[OSD([sQuery(id+"F0.wireOp",EDGE,"E1.bottom")])],"isStart":false});
            fillet(context, id + "F15", {"entities" : qUnion([Q0]), "radius" : 2 * mm, "tangentPropagation" : true, "allowEdgeOverflow" : false});
        }
        {
            var Q0;
            {var subQ0=sQuery(id+"F0.wireOp",EDGE,"E21.filletArc");var subQ1=sQuery(id+"F0.wireOp",EDGE,"E7");var subQ2=sQuery(id+"F0.wireOp",EDGE,"E6");var subQ3=sQuery(id+"F0.wireOp",EDGE,"E5");var subQ4=sQuery(id+"F0.wireOp",EDGE,"E4");var subQ5=sQuery(id+"F0.wireOp",EDGE,"E22.filletArc");var subQ6=sQuery(id+"F0.wireOp",EDGE,"E1.bottom");var subQ7=sQuery(id+"F0.wireOp",EDGE,"E1.right");var subQ8=sQuery(id+"F0.wireOp",EDGE,"E1.top");var subQ9=sQuery(id+"F0.wireOp",EDGE,"E1.left");var subQ10=sQuery(id+"F0.wireOp",EDGE,"E23.filletArc");var subQ11=sQuery(id+"F0.wireOp",EDGE,"E24.filletArc");Q0=makeQuery(id+"F2.boolean.opBoolean","SPLIT",FACE,{"disambiguationData":[TD([makeQuery(id+"F1.opExtrude","SWEPT_FACE",FACE,{"disambiguationData":[OSD([subQ6])]})])],"derivedFrom":makeQuery(id+"F1.opExtrude","CAP_FACE",FACE,{"disambiguationData":[OSD([subQ6,subQ8,subQ9,subQ7,subQ4,subQ3,subQ2,subQ1,subQ0,subQ5,subQ10,subQ11])],"isStart":true})});}
            var sketch = newSketch(context, id + "F16", { "sketchPlane" : qUnion([Q0])});
            skLineSegment(sketch, "E79", {"start": v(0, 74.25) * mm, "end": v(0, 104.25) * mm, "construction": true});
            skCircle(sketch, "E80", {"center": v(0, 104.25) * mm, "radius": 6 * mm});
            skLineSegment(sketch, "E81", {"start": v(-33, 74.25) * mm, "end": v(-15, 92.25) * mm});
            skLineSegment(sketch, "E82", {"start": v(33, 74.25) * mm, "end": v(15, 92.25) * mm});
            skLineSegment(sketch, "E83", {"start": v(15, 92.25) * mm, "end": v(15, 104.25) * mm});
            skLineSegment(sketch, "E84", {"start": v(-15, 92.25) * mm, "end": v(-15, 104.25) * mm});
            skArc(sketch, "E85", {"start": v(15, 104.25) * mm, "mid": v(0, 119.25) * mm, "end": v(-15, 104.25) * mm});
            skLineSegment(sketch, "E86", {"start": v(-74.25, 0) * mm, "end": v(74.25, 0) * mm, "construction": true});
            skLineSegment(sketch, "E87.MirrorCS", {"start": v(33, -74.25) * mm, "end": v(15, -92.25) * mm});
            skLineSegment(sketch, "E88.MirrorCS", {"start": v(15, -92.25) * mm, "end": v(15, -104.25) * mm});
            skArc(sketch, "E89.MirrorCS", {"start": v(15, -104.25) * mm, "mid": v(0, -119.25) * mm, "end": v(-15, -104.25) * mm});
            skLineSegment(sketch, "E90.MirrorCS", {"start": v(-15, -92.25) * mm, "end": v(-15, -104.25) * mm});
            skLineSegment(sketch, "E91.MirrorCS", {"start": v(-33, -74.25) * mm, "end": v(-15, -92.25) * mm});
            skLineSegment(sketch, "E92.MirrorCS", {"start": v(0, -74.25) * mm, "end": v(0, -104.25) * mm, "construction": true});
            skCircle(sketch, "E93.MirrorC", {"center": v(0, -104.25) * mm, "radius": 6 * mm});
            skSolve(sketch);
        }
        {
            var Q0;
            Q0=makeQuery(id+"F16.imprint","IMPRINT",FACE,{"disambiguationData":[TD([[makeQuery(id+"F16.imprint","IMPRINT",EDGE,{"derivedFrom":makeQuery(id+"F1.opExtrude","CAP_EDGE",EDGE,{"disambiguationData":[OSD([sQuery(id+"F0.wireOp",EDGE,"E1.left")])],"isStart":true})}),-1.0]])]});
            var sketch = newSketch(context, id + "F17", { "sketchPlane" : qUnion([Q0])});
            skSolve(sketch);
        }
        {
            var Q0;
            Q0=makeQuery(id+"F16.imprint","IMPRINT",FACE,{"disambiguationData":[TD([[makeQuery(id+"F16.imprint","IMPRINT",EDGE,{"derivedFrom":sQuery(id+"F16.wireOp",EDGE,"E80")}),-1.0]])]});
            var Q1;
            Q1=makeQuery(id+"F16.imprint","IMPRINT",FACE,{"disambiguationData":[TD([[makeQuery(id+"F16.imprint","IMPRINT",EDGE,{"derivedFrom":makeQuery(id+"F1.opExtrude","CAP_EDGE",EDGE,{"disambiguationData":[OSD([sQuery(id+"F0.wireOp",EDGE,"E1.left")])],"isStart":true})}),-1.0]])]});
            var Q2;
            {var subQ0=sQuery(id+"F16.wireOp",EDGE,"E87.MirrorCS");Q2=makeQuery(id+"F16.imprint","IMPRINT",FACE,{"disambiguationData":[TD([[makeQuery(id+"F16.imprint","IMPRINT",EDGE,{"derivedFrom":subQ0}),-1.0]])]});}
            var Q3;
            Q3=makeQuery(id+"F2.opExtrude","CAP_FACE",FACE,{"disambiguationData":[OSD([sQuery(id+"F0.wireOp",EDGE,"E12"),sQuery(id+"F0.wireOp",EDGE,"E13"),sQuery(id+"F0.wireOp",EDGE,"E14"),sQuery(id+"F0.wireOp",EDGE,"E15"),sQuery(id+"F0.wireOp",EDGE,"E17.filletArc"),sQuery(id+"F0.wireOp",EDGE,"E18.filletArc"),sQuery(id+"F0.wireOp",EDGE,"E19.filletArc"),sQuery(id+"F0.wireOp",EDGE,"E20.filletArc"),sQuery(id+"F0.wireOp",EDGE,"E25.0"),sQuery(id+"F0.wireOp",EDGE,"E25.1"),sQuery(id+"F0.wireOp",EDGE,"E25.2"),sQuery(id+"F0.wireOp",EDGE,"E25.3"),sQuery(id+"F0.wireOp",EDGE,"E25.4"),sQuery(id+"F0.wireOp",EDGE,"E25.5"),sQuery(id+"F0.wireOp",EDGE,"E25.6"),sQuery(id+"F0.wireOp",EDGE,"E25.7")])],"isStart":false});
            extrude(context, id + "F18", {"entities" : qUnion([Q0, Q1, Q2]), "endBound" : BoundingType.UP_TO_SURFACE, "endBoundEntityFace" : qUnion([Q3]), "depth" : 25 * mm});
        }
    });
